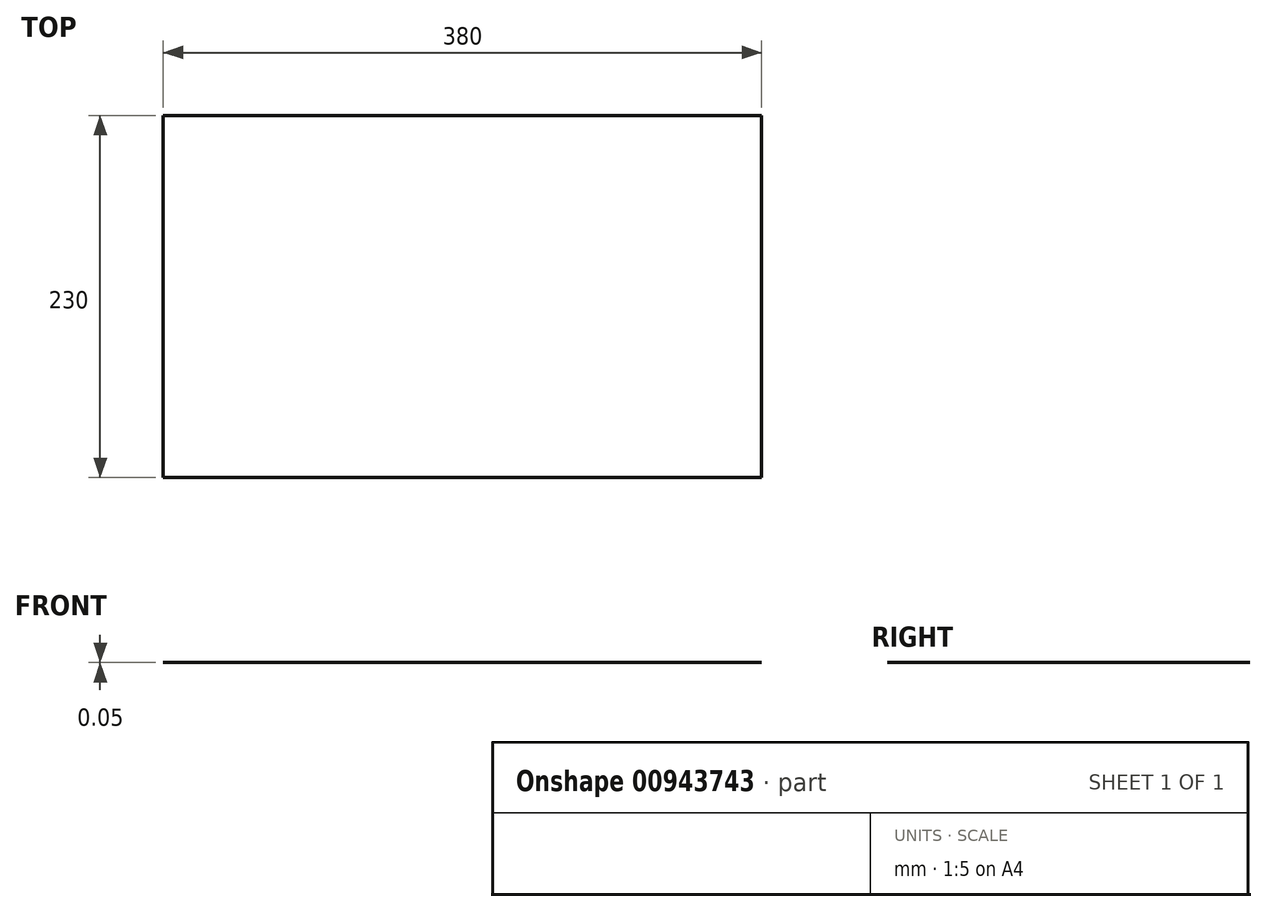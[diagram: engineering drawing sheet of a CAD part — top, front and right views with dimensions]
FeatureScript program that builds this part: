
annotation { "Feature Type Name" : "Feature", "Feature Type Description" : "" }
export const myFeature = defineFeature(function(context is Context, id is Id, definition is map)
    precondition{}
    {
        {
            var Q0;
            Q0=qCreatedBy(makeId("Top.planeOp"),FACE);
            var sketch = newSketch(context, id + "F0", { "sketchPlane" : qUnion([Q0])});
            skLineSegment(sketch, "E0.bottom", {"start": v(190, -115) * mm, "end": v(-190, -115) * mm});
            skLineSegment(sketch, "E0.top", {"start": v(190, 115) * mm, "end": v(-190, 115) * mm});
            skLineSegment(sketch, "E0.left", {"start": v(190, -115) * mm, "end": v(190, 115) * mm});
            skLineSegment(sketch, "E0.right", {"start": v(-190, -115) * mm, "end": v(-190, 115) * mm});
            skPoint(sketch, "E0.middle", {"position": v(0, 0) * mm});
            skSolve(sketch);
        }
        {
            var Q0;
            Q0 = qSketchRegion(id + "F0", true);
            extrude(context, id + "F1", {"entities" : qUnion([Q0]), "depth" : 0.05 * mm, "offsetDistance" : 25 * mm});
        }
    });
